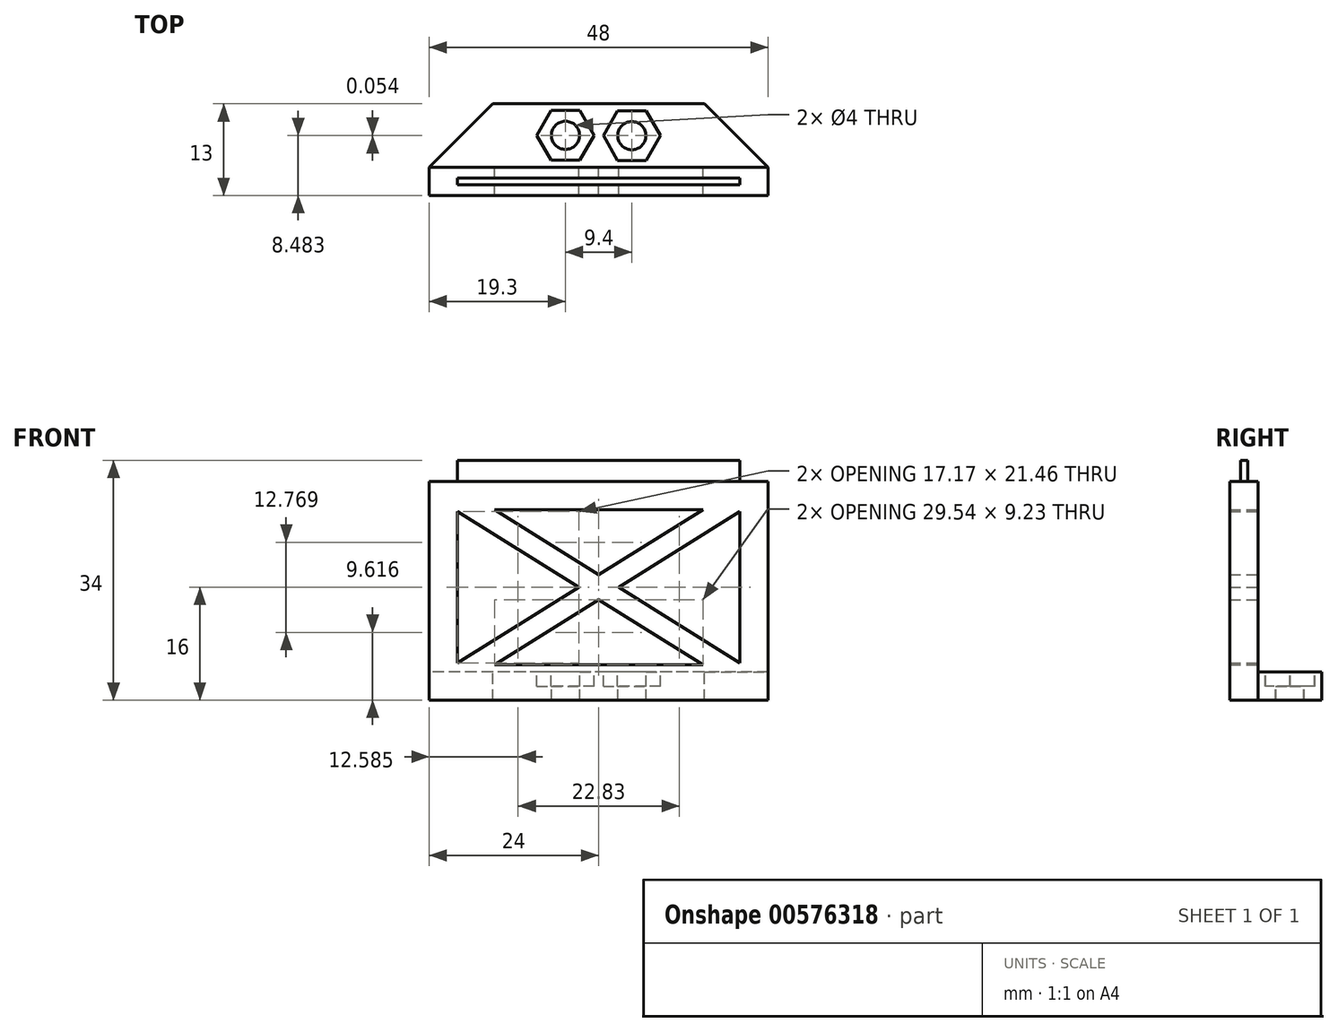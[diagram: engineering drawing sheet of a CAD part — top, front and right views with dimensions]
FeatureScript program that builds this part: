
annotation { "Feature Type Name" : "Feature", "Feature Type Description" : "" }
export const myFeature = defineFeature(function(context is Context, id is Id, definition is map)
    precondition{}
    {
        {
            var Q0;
            Q0=qCreatedBy(makeId("Front.planeOp"),FACE);
            var sketch = newSketch(context, id + "F0", { "sketchPlane" : qUnion([Q0])});
            skLineSegment(sketch, "E0.bottom", {"start": v(-25.07, 0) * mm, "end": v(22.93, 0) * mm});
            skLineSegment(sketch, "E0.top", {"start": v(-25.07, 30) * mm, "end": v(22.93, 30) * mm});
            skLineSegment(sketch, "E0.left", {"start": v(-25.07, 0) * mm, "end": v(-25.07, 30) * mm});
            skLineSegment(sketch, "E0.right", {"start": v(22.93, 0) * mm, "end": v(22.93, 30) * mm});
            skLineSegment(sketch, "E1", {"start": v(-25.07, 30) * mm, "end": v(22.93, 0) * mm, "construction": true});
            skLineSegment(sketch, "E2", {"start": v(-25.07, 0) * mm, "end": v(22.93, 30) * mm, "construction": true});
            skLineSegment(sketch, "E3", {"start": v(-1.07, 30) * mm, "end": v(-1.07, 0) * mm, "construction": true});
            skLineSegment(sketch, "E4", {"start": v(-25.07, 15) * mm, "end": v(22.93, 15) * mm, "construction": true});
            skLineSegment(sketch, "E5", {"start": v(-22.24, 30) * mm, "end": v(-1.07, 16.77) * mm, "construction": true});
            skLineSegment(sketch, "E6", {"start": v(-25.07, 28.23) * mm, "end": v(-3.9, 15) * mm, "construction": true});
            skLineSegment(sketch, "E7", {"start": v(20.1, 30) * mm, "end": v(-1.07, 16.77) * mm, "construction": true});
            skLineSegment(sketch, "E8", {"start": v(-3.9, 15) * mm, "end": v(-25.07, 1.77) * mm, "construction": true});
            skLineSegment(sketch, "E9", {"start": v(-22.24, 0) * mm, "end": v(-1.07, 13.23) * mm, "construction": true});
            skLineSegment(sketch, "E10", {"start": v(22.93, 28.23) * mm, "end": v(1.76, 15) * mm, "construction": true});
            skLineSegment(sketch, "E11", {"start": v(1.76, 15) * mm, "end": v(22.93, 1.77) * mm, "construction": true});
            skLineSegment(sketch, "E12", {"start": v(-1.07, 13.23) * mm, "end": v(20.1, 0) * mm, "construction": true});
            skLineSegment(sketch, "E13", {"start": v(-21.07, 30) * mm, "end": v(-21.07, 0) * mm, "construction": true});
            skLineSegment(sketch, "E14", {"start": v(18.93, 30) * mm, "end": v(18.93, 0) * mm, "construction": true});
            skLineSegment(sketch, "E15", {"start": v(-25.07, 4) * mm, "end": v(22.93, 4) * mm, "construction": true});
            skLineSegment(sketch, "E16", {"start": v(-21.07, 25.73) * mm, "end": v(-21.07, 4.27) * mm});
            skLineSegment(sketch, "E17", {"start": v(-15.84, 4) * mm, "end": v(13.7, 4) * mm});
            skLineSegment(sketch, "E18", {"start": v(18.93, 4.27) * mm, "end": v(18.93, 25.73) * mm});
            skLineSegment(sketch, "E19", {"start": v(-15.84, 26) * mm, "end": v(-1.07, 16.77) * mm});
            skLineSegment(sketch, "E20", {"start": v(-3.9, 15) * mm, "end": v(-21.07, 25.73) * mm});
            skLineSegment(sketch, "E21", {"start": v(-3.9, 15) * mm, "end": v(-21.07, 4.27) * mm});
            skLineSegment(sketch, "E22", {"start": v(-15.84, 4) * mm, "end": v(-1.07, 13.23) * mm});
            skLineSegment(sketch, "E23", {"start": v(-1.07, 13.23) * mm, "end": v(13.7, 4) * mm});
            skLineSegment(sketch, "E24", {"start": v(18.93, 4.27) * mm, "end": v(1.76, 15) * mm});
            skLineSegment(sketch, "E25", {"start": v(1.76, 15) * mm, "end": v(18.93, 25.73) * mm});
            skLineSegment(sketch, "E26", {"start": v(-15.84, 26) * mm, "end": v(13.7, 26) * mm});
            skLineSegment(sketch, "E27", {"start": v(13.7, 26) * mm, "end": v(-1.07, 16.77) * mm});
            skSolve(sketch);
        }
        {
            var Q0;
            Q0=makeQuery(id+"F0.imprint","IMPRINT",FACE,{"disambiguationData":[TD([[makeQuery(id+"F0.imprint","IMPRINT",EDGE,{"derivedFrom":sQuery(id+"F0.wireOp",EDGE,"E0.bottom")}),1.0]])]});
            extrude(context, id + "F1", {"entities" : qUnion([Q0]), "depth" : 4 * mm, "offsetDistance" : 25 * mm});
        }
        {
            var Q0;
            Q0=makeQuery(id+"F1.opExtrude","SWEPT_FACE",FACE,{"disambiguationData":[OSD([sQuery(id+"F0.wireOp",EDGE,"E0.bottom")])]});
            extrude(context, id + "F2", {"entities" : qUnion([Q0]), "operationType" : NewBodyOperationType.ADD, "depth" : 1 * mm, "offsetDistance" : 25 * mm});
        }
        {
            var Q0;
            {var subQ0=sQuery(id+"Fv1Ph5lZ28bCs0f_1.wireOp",EDGE,"A9J8lcfE-D3E1-5bLC-v4m9-Y004XlXRwedo");var subQ1=sQuery(id+"F0.wireOp",EDGE,"E0.top");Q0=makeQuery(id+"F79FwnqT1oFWdj9_1.boolean.opBoolean","MERGE",FACE,{"derivedFrom":[makeQuery(id+"F1.opExtrude","SWEPT_FACE",FACE,{"disambiguationData":[OSD([subQ1])]}),makeQuery(id+"F79FwnqT1oFWdj9_1.opExtrude","CAP_FACE",FACE,{"disambiguationData":[OSD([subQ1,sQuery(id+"F0.wireOp",EDGE,"E0.left"),subQ0,sQuery(id+"Fv1Ph5lZ28bCs0f_1.wireOp",EDGE,"ZuAYeMef-ndJL-GfuJ-usOO-NELdWAyxJQJv")])],"isStart":true}),makeQuery(id+"F79FwnqT1oFWdj9_1.opExtrude","CAP_FACE",FACE,{"disambiguationData":[OSD([subQ1,sQuery(id+"F0.wireOp",EDGE,"E0.right"),subQ0,sQuery(id+"Fv1Ph5lZ28bCs0f_1.wireOp",EDGE,"7GaJ3ACz-FEC6-0tyE-cT2s-0WhtsvvSRLuo")])],"isStart":true})]});}
            var sketch = newSketch(context, id + "F3", { "sketchPlane" : qUnion([Q0])});
            skLineSegment(sketch, "E28", {"start": v(-1.07, -4) * mm, "end": v(-1.07, 0) * mm, "construction": true});
            skLineSegment(sketch, "E29.bottom", {"start": v(18.93, -2.5) * mm, "end": v(-21.07, -2.5) * mm});
            skLineSegment(sketch, "E29.top", {"start": v(18.93, -1.5) * mm, "end": v(-21.07, -1.5) * mm});
            skLineSegment(sketch, "E29.left", {"start": v(18.93, -2.5) * mm, "end": v(18.93, -1.5) * mm});
            skLineSegment(sketch, "E29.right", {"start": v(-21.07, -2.5) * mm, "end": v(-21.07, -1.5) * mm});
            skPoint(sketch, "E29.middle", {"position": v(-1.07, -2) * mm});
            skSolve(sketch);
        }
        {
            var Q0;
            Q0=makeQuery(id+"F3.imprint","IMPRINT",FACE,{"disambiguationData":[TD([[makeQuery(id+"F3.imprint","IMPRINT",EDGE,{"derivedFrom":sQuery(id+"F3.wireOp",EDGE,"E29.bottom")}),-1.0]])]});
            extrude(context, id + "F4", {"entities" : qUnion([Q0]), "operationType" : NewBodyOperationType.ADD, "depth" : 3 * mm, "offsetDistance" : 25 * mm});
        }
        {
            var Q0;
            {var subQ0=sQuery(id+"F0.wireOp",EDGE,"E0.bottom");Q0=makeQuery(id+"F2.boolean.opBoolean","MERGE",FACE,{"derivedFrom":[makeQuery(id+"F1.opExtrude","CAP_FACE",FACE,{"disambiguationData":[OSD([subQ0,sQuery(id+"F0.wireOp",EDGE,"E0.top"),sQuery(id+"F0.wireOp",EDGE,"E0.left"),sQuery(id+"F0.wireOp",EDGE,"E0.right"),sQuery(id+"F0.wireOp",EDGE,"E16"),sQuery(id+"F0.wireOp",EDGE,"E17"),sQuery(id+"F0.wireOp",EDGE,"E18"),sQuery(id+"F0.wireOp",EDGE,"E19"),sQuery(id+"F0.wireOp",EDGE,"E20"),sQuery(id+"F0.wireOp",EDGE,"E21"),sQuery(id+"F0.wireOp",EDGE,"E22"),sQuery(id+"F0.wireOp",EDGE,"E23"),sQuery(id+"F0.wireOp",EDGE,"E24"),sQuery(id+"F0.wireOp",EDGE,"E25"),sQuery(id+"F0.wireOp",EDGE,"E26"),sQuery(id+"F0.wireOp",EDGE,"E27")])],"isStart":true}),makeQuery(id+"F2.opExtrude","SWEPT_FACE",FACE,{"disambiguationData":[OSD([subQ0]),TDD([makeQuery(id+"F1.opExtrude","CAP_EDGE",EDGE,{"disambiguationData":[OSD([subQ0])],"isStart":true})])]})]});}
            var sketch = newSketch(context, id + "F5", { "sketchPlane" : qUnion([Q0])});
            skLineSegment(sketch, "E30.bottom", {"start": v(-22.93, -1) * mm, "end": v(25.07, -1) * mm});
            skLineSegment(sketch, "E30.top", {"start": v(-22.93, 3) * mm, "end": v(25.07, 3) * mm});
            skLineSegment(sketch, "E30.left", {"start": v(-22.93, -1) * mm, "end": v(-22.93, 3) * mm});
            skLineSegment(sketch, "E30.right", {"start": v(25.07, -1) * mm, "end": v(25.07, 3) * mm});
            skSolve(sketch);
        }
        {
            var Q0;
            Q0=makeQuery(id+"F5.imprint","IMPRINT",FACE,{"disambiguationData":[TD([[makeQuery(id+"F5.imprint","IMPRINT",EDGE,{"derivedFrom":sQuery(id+"F5.wireOp",EDGE,"E30.bottom")}),-1.0]])]});
            extrude(context, id + "F6", {"entities" : qUnion([Q0]), "operationType" : NewBodyOperationType.ADD, "depth" : 9 * mm, "offsetDistance" : 25 * mm});
        }
        {
            var Q0;
            Q0=makeQuery(id+"F6.opExtrude","SWEPT_FACE",FACE,{"disambiguationData":[OSD([sQuery(id+"F5.wireOp",EDGE,"E30.top")])]});
            var sketch = newSketch(context, id + "F7", { "sketchPlane" : qUnion([Q0])});
            skPoint(sketch, "E31", {"position": v(-5.77, 4.54) * mm});
            skPoint(sketch, "E32", {"position": v(3.63, 4.48) * mm});
            skLineSegment(sketch, "E33", {"start": v(-5.77, 4.54) * mm, "end": v(-25.07, 4.54) * mm, "construction": true});
            skLineSegment(sketch, "E34", {"start": v(3.63, 4.48) * mm, "end": v(22.93, 4.48) * mm, "construction": true});
            skCircle(sketch, "E35", {"center": v(-5.77, 4.54) * mm, "radius": 2 * mm});
            skCircle(sketch, "E36", {"center": v(3.63, 4.48) * mm, "radius": 2 * mm});
            skCircle(sketch, "E37.cCircle", {"center": v(-5.77, 4.54) * mm, "radius": 3.5 * mm, "construction": true});
            skLineSegment(sketch, "E37.0", {"start": v(-1.73, 4.54) * mm, "end": v(-3.75, 1.04) * mm});
            skLineSegment(sketch, "E37.1", {"start": v(-3.75, 1.04) * mm, "end": v(-7.8, 1.04) * mm});
            skLineSegment(sketch, "E37.2", {"start": v(-7.8, 1.04) * mm, "end": v(-9.81, 4.54) * mm});
            skLineSegment(sketch, "E37.3", {"start": v(-9.81, 4.54) * mm, "end": v(-7.8, 8.04) * mm});
            skLineSegment(sketch, "E37.4", {"start": v(-7.8, 8.04) * mm, "end": v(-3.75, 8.04) * mm});
            skLineSegment(sketch, "E37.5", {"start": v(-3.75, 8.04) * mm, "end": v(-1.73, 4.54) * mm});
            skPoint(sketch, "E37.0.midPoint", {"position": v(-2.74, 2.79) * mm});
            skCircle(sketch, "E38.cCircle", {"center": v(3.63, 4.48) * mm, "radius": 3.5 * mm, "construction": true});
            skLineSegment(sketch, "E38.0", {"start": v(7.67, 4.48) * mm, "end": v(5.65, 0.98) * mm});
            skLineSegment(sketch, "E38.1", {"start": v(5.65, 0.98) * mm, "end": v(1.6, 0.98) * mm});
            skLineSegment(sketch, "E38.2", {"start": v(1.6, 0.98) * mm, "end": v(-0.41, 4.48) * mm});
            skLineSegment(sketch, "E38.3", {"start": v(-0.41, 4.48) * mm, "end": v(1.6, 7.98) * mm});
            skLineSegment(sketch, "E38.4", {"start": v(1.6, 7.98) * mm, "end": v(5.65, 7.98) * mm});
            skLineSegment(sketch, "E38.5", {"start": v(5.65, 7.98) * mm, "end": v(7.67, 4.48) * mm});
            skPoint(sketch, "E38.0.midPoint", {"position": v(6.66, 2.73) * mm});
            skSolve(sketch);
        }
        {
            var Q0;
            Q0=makeQuery(id+"F7.imprint","IMPRINT",FACE,{"disambiguationData":[TD([[makeQuery(id+"F7.imprint","IMPRINT",EDGE,{"derivedFrom":sQuery(id+"F7.wireOp",EDGE,"E35")}),1.0]])]});
            var Q1;
            Q1=makeQuery(id+"F7.imprint","IMPRINT",FACE,{"disambiguationData":[TD([[makeQuery(id+"F7.imprint","IMPRINT",EDGE,{"derivedFrom":sQuery(id+"F7.wireOp",EDGE,"E36")}),1.0]])]});
            extrude(context, id + "F8", {"entities" : qUnion([Q0, Q1]), "operationType" : NewBodyOperationType.REMOVE, "oppositeDirection" : true, "depth" : 4 * mm, "offsetDistance" : 25 * mm});
        }
        {
            var Q0;
            Q0=makeQuery(id+"F7.imprint","IMPRINT",FACE,{"disambiguationData":[TD([[makeQuery(id+"F7.imprint","IMPRINT",EDGE,{"derivedFrom":sQuery(id+"F7.wireOp",EDGE,"E35")}),-1.0]])]});
            var Q1;
            Q1=makeQuery(id+"F7.imprint","IMPRINT",FACE,{"disambiguationData":[TD([[makeQuery(id+"F7.imprint","IMPRINT",EDGE,{"derivedFrom":sQuery(id+"F7.wireOp",EDGE,"E36")}),-1.0]])]});
            extrude(context, id + "F9", {"entities" : qUnion([Q0, Q1]), "operationType" : NewBodyOperationType.REMOVE, "oppositeDirection" : true, "depth" : 2 * mm, "offsetDistance" : 25 * mm});
        }
        {
            var Q0;
            Q0=makeQuery(id+"F6.opExtrude","SWEPT_FACE",FACE,{"disambiguationData":[OSD([sQuery(id+"F5.wireOp",EDGE,"E30.top")])]});
            var sketch = newSketch(context, id + "F10", { "sketchPlane" : qUnion([Q0])});
            skLineSegment(sketch, "E39", {"start": v(-25.07, 0) * mm, "end": v(-25.07, 9) * mm, "construction": true});
            skLineSegment(sketch, "E40", {"start": v(-25.07, 9) * mm, "end": v(-16.07, 9) * mm, "construction": true});
            skLineSegment(sketch, "E41", {"start": v(-16.07, 9) * mm, "end": v(-25.07, 0) * mm});
            skLineSegment(sketch, "E42", {"start": v(22.93, 9) * mm, "end": v(22.93, 0) * mm, "construction": true});
            skLineSegment(sketch, "E43", {"start": v(22.93, 9) * mm, "end": v(13.93, 9) * mm, "construction": true});
            skLineSegment(sketch, "E44", {"start": v(13.93, 9) * mm, "end": v(22.93, 0) * mm});
            skSolve(sketch);
        }
        {
            var Q0;
            {var subQ0=sQuery(id+"F10.wireOp",EDGE,"E41");Q0=makeQuery(id+"F10.imprint","IMPRINT",FACE,{"disambiguationData":[TD([[makeQuery(id+"F10.imprint","IMPRINT",EDGE,{"derivedFrom":subQ0}),-1.0]])]});}
            var Q1;
            {var subQ0=sQuery(id+"F10.wireOp",EDGE,"E44");Q1=makeQuery(id+"F10.imprint","IMPRINT",FACE,{"disambiguationData":[TD([[makeQuery(id+"F10.imprint","IMPRINT",EDGE,{"derivedFrom":subQ0}),1.0]])]});}
            extrude(context, id + "F11", {"entities" : qUnion([Q0, Q1]), "operationType" : NewBodyOperationType.REMOVE, "oppositeDirection" : true, "depth" : 4 * mm, "offsetDistance" : 25 * mm});
        }
    });
